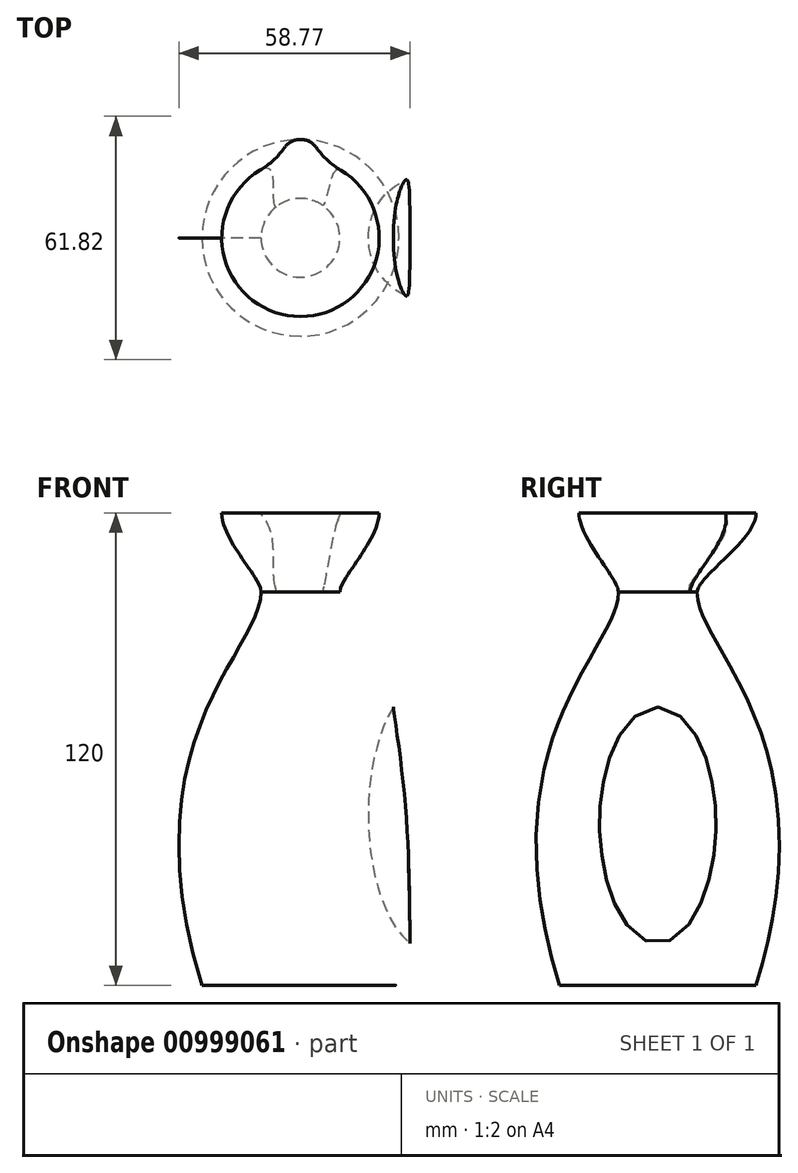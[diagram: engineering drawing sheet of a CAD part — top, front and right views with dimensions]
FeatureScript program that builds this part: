
annotation { "Feature Type Name" : "Feature", "Feature Type Description" : "" }
export const myFeature = defineFeature(function(context is Context, id is Id, definition is map)
    precondition{}
    {
        {
            var Q0;
            Q0=qCreatedBy(makeId("Front.planeOp"),FACE);
            var sketch = newSketch(context, id + "F0", { "sketchPlane" : qUnion([Q0])});
            skFitSpline(sketch, "E0", {"points": [v(-10, 100) * mm, v(-25, 0) * mm], "startDerivative": vector(0, -45.3) * mm, "endDerivative": vector(58.02, -188.96) * mm});
            skLineSegment(sketch, "E1", {"start": v(-10, 100) * mm, "end": v(-10, 57.37) * mm, "construction": true});
            skLineSegment(sketch, "E2", {"start": v(-25, 0) * mm, "end": v(0, 0) * mm});
            skLineSegment(sketch, "E3", {"start": v(0, 0) * mm, "end": v(0, 100) * mm});
            skLineSegment(sketch, "E4", {"start": v(0, 100) * mm, "end": v(-10, 100) * mm});
            skSolve(sketch);
        }
        {
            var Q0;
            Q0=makeQuery(id+"F0.imprint","IMPRINT",FACE,{"disambiguationData":[TD([[makeQuery(id+"F0.imprint","IMPRINT",EDGE,{"derivedFrom":sQuery(id+"F0.wireOp",EDGE,"E0")}),1.0]])]});
            var Q1;
            Q1=sQuery(id+"F0.wireOp",EDGE,"E3");
            revolve(context, id + "F1", {"surfaceOperationType" : NewSurfaceOperationType.NEW, "entities" : qUnion([Q0]), "axis" : qUnion([Q1]), "revolveType" : RevolveType.FULL});
        }
        {
            var Q0;
            Q0=makeQuery(id+"F1.opRevolve","SWEPT_FACE",FACE,{"disambiguationData":[OSD([sQuery(id+"F0.wireOp",EDGE,"E4")])]});
            cPlane(context, id + "F2", {"entities" : qUnion([Q0]), "cplaneType" : CPlaneType.OFFSET, "offset" : 20 * mm, "width" : 150 * mm, "height" : 150 * mm});
        }
        {
            var Q0;
            Q0=qCreatedBy(id+"F2.planeOp",FACE);
            var sketch = newSketch(context, id + "F3", { "sketchPlane" : qUnion([Q0])});
            skCircle(sketch, "E5", {"center": v(0, 0) * mm, "radius": 20 * mm});
            skSolve(sketch);
        }
        {
            var Q1;
            Q1=makeQuery(id+"F3.imprint","IMPRINT",FACE,{"disambiguationData":[TD([[makeQuery(id+"F3.imprint","IMPRINT",EDGE,{"derivedFrom":sQuery(id+"F3.wireOp",EDGE,"E5")}),1.0]])]});
            var Q2;
            Q2=makeQuery(id+"F1.opRevolve","SWEPT_FACE",FACE,{"disambiguationData":[OSD([sQuery(id+"F0.wireOp",EDGE,"E4")])]});
            loft(context, id + "F4", {"operationType" : NewBodyOperationType.ADD, "startCondition" : LoftEndDerivativeType.NORMAL_TO_PROFILE, "startMagnitude" : 1, "endCondition" : LoftEndDerivativeType.MATCH_TANGENT, "endMagnitude" : 0.5, "sheetProfilesArray" : [{ "sheetProfileEntities" : qUnion([Q1]) }, { "sheetProfileEntities" : qUnion([Q2]) }]});
        }
        {
            var Q0;
            Q0=makeQuery(id+"F4.opLoft","CAP_FACE",FACE,{"disambiguationData":[OSD([makeQuery(id+"F3.imprint","IMPRINT",FACE,{"disambiguationData":[TD([[makeQuery(id+"F3.imprint","IMPRINT",EDGE,{"derivedFrom":sQuery(id+"F3.wireOp",EDGE,"E5")}),1.0]])]})])],"isStart":true});
            var sketch = newSketch(context, id + "F5", { "sketchPlane" : qUnion([Q0])});
            skArc(sketch, "E6", {"start": v(4.1, 22.88) * mm, "mid": v(0, 25) * mm, "end": v(-4.1, 22.88) * mm});
            skArc(sketch, "E7", {"start": v(-10.23, 17.19) * mm, "mid": v(-17.39, 9.89) * mm, "end": v(-20, 0) * mm});
            skPoint(sketch, "E8.visualSharp", {"position": v(-4.96, 19.38) * mm});
            skArc(sketch, "E8.filletArc", {"start": v(-10.23, 17.19) * mm, "mid": v(-6.86, 19.7) * mm, "end": v(-4.1, 22.88) * mm});
            skPoint(sketch, "E9.visualSharp", {"position": v(4.96, 19.38) * mm});
            skArc(sketch, "E9.filletArc", {"start": v(4.1, 22.88) * mm, "mid": v(6.86, 19.7) * mm, "end": v(10.23, 17.19) * mm});
            skLineSegment(sketch, "E10", {"start": v(-20, 0) * mm, "end": v(20, 0) * mm});
            skPoint(sketch, "E11.orphan", {"position": v(-22.16, 0) * mm});
            skArc(sketch, "E12.trimOffspring", {"start": v(20, 0) * mm, "mid": v(17.39, 9.89) * mm, "end": v(10.23, 17.19) * mm});
            skSolve(sketch);
        }
        {
            var Q0;
            Q0=qCreatedBy(id+"F2.planeOp",FACE);
            cPlane(context, id + "F6", {"entities" : qUnion([Q0]), "cplaneType" : CPlaneType.OFFSET, "offset" : 20 * mm, "oppositeDirection" : true, "width" : 150 * mm, "height" : 150 * mm});
        }
        {
            var Q0;
            Q0=qCreatedBy(id+"F6.planeOp",FACE);
            var sketch = newSketch(context, id + "F7", { "sketchPlane" : qUnion([Q0])});
            skCircle(sketch, "E13", {"center": v(0, 0) * mm, "radius": 10 * mm});
            skSolve(sketch);
        }
        {
            var Q1;
            Q1 = qSketchRegion(id + "F5", true);
            var Q2;
            Q2 = qSketchRegion(id + "F7", true);
            loft(context, id + "F8", {"operationType" : NewBodyOperationType.ADD, "startCondition" : LoftEndDerivativeType.NORMAL_TO_PROFILE, "startMagnitude" : 1, "endCondition" : LoftEndDerivativeType.NORMAL_TO_PROFILE, "endMagnitude" : 0.5, "sheetProfilesArray" : [{ "sheetProfileEntities" : qUnion([Q1]) }, { "sheetProfileEntities" : qUnion([Q2]) }]});
        }
        {
            var Q0;
            Q0=qCreatedBy(makeId("Front.planeOp"),FACE);
            var sketch = newSketch(context, id + "F9", { "sketchPlane" : qUnion([Q0])});
            skEllipticalArc(sketch, "E14", {});
            skLineSegment(sketch, "E15", {"start": v(33.37, 77.79) * mm, "end": v(33.37, 8.58) * mm});
            const initialGuessF9  = {"E14": [0.03336871415376663, 0.0431818962097168, 0, -1, 0.03460458852350712, 0.01613447354420711, 3.141592653589793, 0]};
            skSetInitialGuess(sketch, initialGuessF9);
            skSolve(sketch);
        }
        {
            var Q0;
            Q0=makeQuery(id+"F9.imprint","IMPRINT",FACE,{"disambiguationData":[TD([[makeQuery(id+"F9.imprint","IMPRINT",EDGE,{"derivedFrom":sQuery(id+"F9.wireOp",EDGE,"E14")}),1.0]])]});
            var Q1;
            Q1=sQuery(id+"F9.wireOp",EDGE,"E15");
            revolve(context, id + "F10", {"operationType" : NewBodyOperationType.REMOVE, "surfaceOperationType" : NewSurfaceOperationType.NEW, "entities" : qUnion([Q0]), "axis" : qUnion([Q1]), "revolveType" : RevolveType.FULL, "oppositeDirection" : true});
        }
    });
